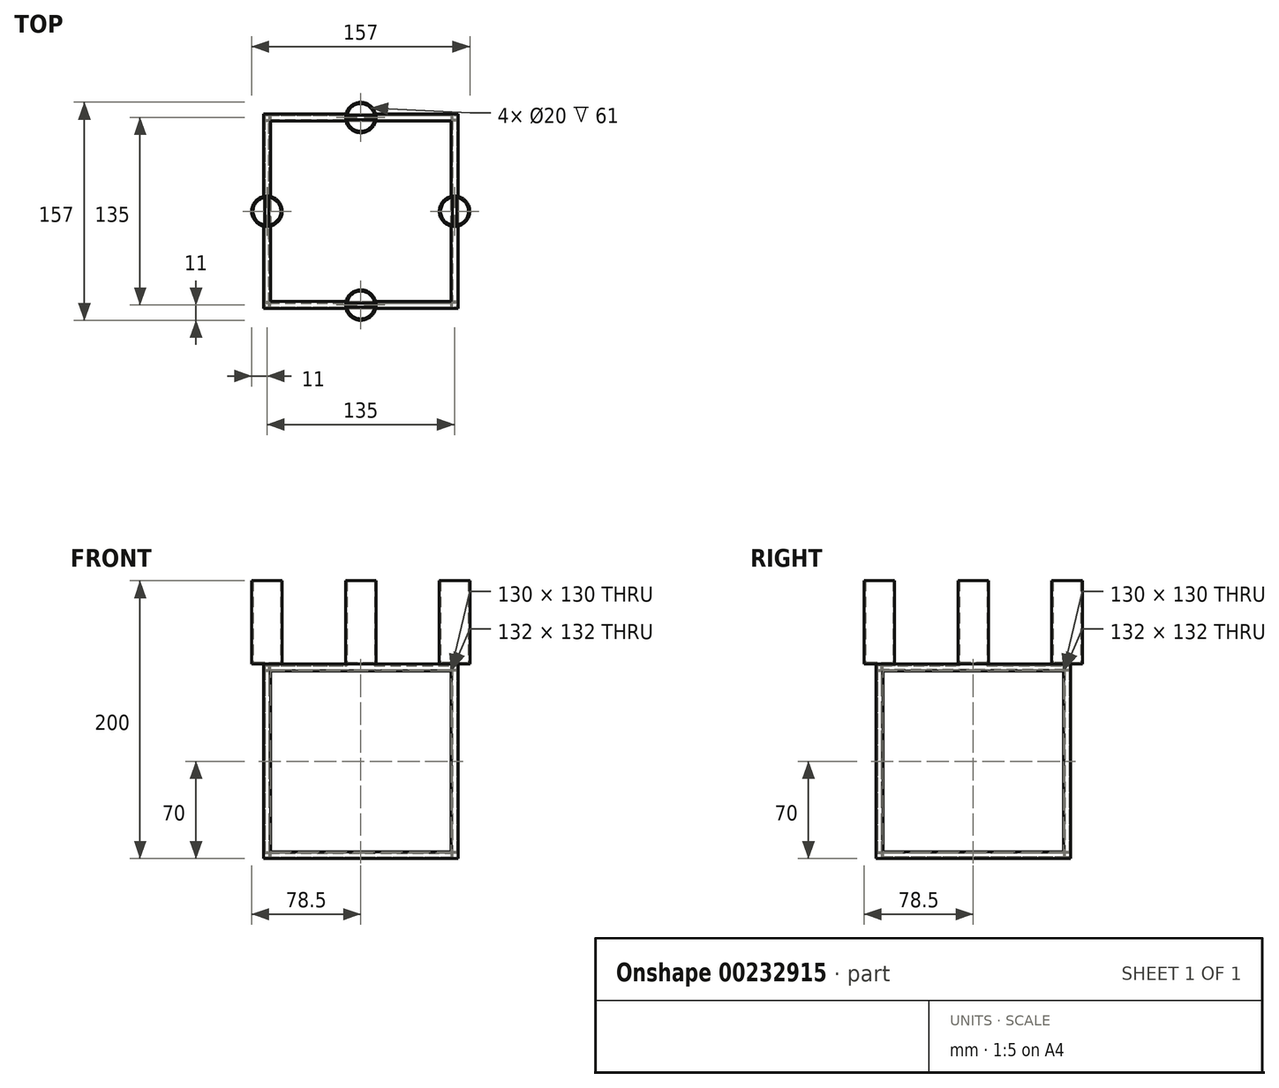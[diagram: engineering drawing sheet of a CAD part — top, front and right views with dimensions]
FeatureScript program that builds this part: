
annotation { "Feature Type Name" : "Feature", "Feature Type Description" : "" }
export const myFeature = defineFeature(function(context is Context, id is Id, definition is map)
    precondition{}
    {
        {
            var Q0;
            Q0=qCreatedBy(makeId("Top.planeOp"),FACE);
            var sketch = newSketch(context, id + "F0", { "sketchPlane" : qUnion([Q0])});
            skLineSegment(sketch, "E0.bottom", {"start": v(-70, 70) * mm, "end": v(70, 70) * mm});
            skLineSegment(sketch, "E0.top", {"start": v(-70, -70) * mm, "end": v(70, -70) * mm});
            skLineSegment(sketch, "E0.left", {"start": v(-70, 70) * mm, "end": v(-70, -70) * mm});
            skLineSegment(sketch, "E0.right", {"start": v(70, 70) * mm, "end": v(70, -70) * mm});
            skPoint(sketch, "E0.middle", {"position": v(0, 0) * mm});
            skLineSegment(sketch, "E1.0", {"start": v(-65, 65) * mm, "end": v(-65, -65) * mm});
            skLineSegment(sketch, "E1.1", {"start": v(-65, 65) * mm, "end": v(65, 65) * mm});
            skLineSegment(sketch, "E1.2", {"start": v(65, 65) * mm, "end": v(65, -65) * mm});
            skLineSegment(sketch, "E1.3", {"start": v(-65, -65) * mm, "end": v(65, -65) * mm});
            skLineSegment(sketch, "E2", {"start": v(-65, 65) * mm, "end": v(-70, 65) * mm});
            skLineSegment(sketch, "E3", {"start": v(-65, 65) * mm, "end": v(-65, 70) * mm});
            skLineSegment(sketch, "E4", {"start": v(65, 65) * mm, "end": v(70, 65) * mm});
            skLineSegment(sketch, "E5", {"start": v(65, 65) * mm, "end": v(65, 70) * mm});
            skLineSegment(sketch, "E6", {"start": v(65, 70) * mm, "end": v(65.55, 70.06) * mm});
            skLineSegment(sketch, "E7", {"start": v(65, -65) * mm, "end": v(70, -65) * mm});
            skLineSegment(sketch, "E8", {"start": v(65, -65) * mm, "end": v(65, -70) * mm});
            skLineSegment(sketch, "E9", {"start": v(-65, -65) * mm, "end": v(-70, -65) * mm});
            skLineSegment(sketch, "E10", {"start": v(-65, -65) * mm, "end": v(-65, -70) * mm});
            skLineSegment(sketch, "E11", {"start": v(-70, 65) * mm, "end": v(-70, 70) * mm});
            skLineSegment(sketch, "E12", {"start": v(-65, 70) * mm, "end": v(-65, 65) * mm});
            skLineSegment(sketch, "E13", {"start": v(-70, -70) * mm, "end": v(-70, -65) * mm});
            skLineSegment(sketch, "E14", {"start": v(65, -70) * mm, "end": v(70, -70) * mm});
            skLineSegment(sketch, "E15", {"start": v(70, 65) * mm, "end": v(70, 70) * mm});
            skSolve(sketch);
        }
        {
            var Q0;
            {var subQ4=sQuery(id+"F0.wireOp",EDGE,"E4");Q0=makeQuery(id+"F0.imprint","IMPRINT",FACE,{"disambiguationData":[TD([[makeQuery(id+"F0.imprint","IMPRINT",EDGE,{"derivedFrom":subQ4}),1.0]])]});}
            var Q1;
            {var subQ4=sQuery(id+"F0.wireOp",EDGE,"E9");Q1=makeQuery(id+"F0.imprint","IMPRINT",FACE,{"disambiguationData":[TD([[makeQuery(id+"F0.imprint","IMPRINT",EDGE,{"derivedFrom":subQ4}),1.0]])]});}
            var Q2;
            {var subQ4=sQuery(id+"F0.wireOp",EDGE,"E7");Q2=makeQuery(id+"F0.imprint","IMPRINT",FACE,{"disambiguationData":[TD([[makeQuery(id+"F0.imprint","IMPRINT",EDGE,{"derivedFrom":subQ4}),-1.0]])]});}
            var Q3;
            Q3=makeQuery(id+"F0.imprint","IMPRINT",FACE,{"disambiguationData":[TD([[makeQuery(id+"F0.imprint","IMPRINT",EDGE,{"derivedFrom":sQuery(id+"F0.wireOp",EDGE,"E1.1")}),1.0]])]});
            var Q4;
            Q4=makeQuery(id+"F0.imprint","IMPRINT",FACE,{"disambiguationData":[TD([[makeQuery(id+"F0.imprint","IMPRINT",EDGE,{"derivedFrom":sQuery(id+"F0.wireOp",EDGE,"E1.3")}),-1.0]])]});
            var Q5;
            Q5=makeQuery(id+"F0.imprint","IMPRINT",FACE,{"disambiguationData":[TD([[makeQuery(id+"F0.imprint","IMPRINT",EDGE,{"derivedFrom":sQuery(id+"F0.wireOp",EDGE,"E1.0")}),-1.0]])]});
            var Q6;
            Q6=makeQuery(id+"F0.imprint","IMPRINT",FACE,{"disambiguationData":[TD([[makeQuery(id+"F0.imprint","IMPRINT",EDGE,{"derivedFrom":sQuery(id+"F0.wireOp",EDGE,"E1.2")}),1.0]])]});
            var Q7;
            Q7=makeQuery(id+"F0.imprint","IMPRINT",FACE,{"disambiguationData":[TD([[makeQuery(id+"F0.imprint","IMPRINT",EDGE,{"derivedFrom":sQuery(id+"F0.wireOp",EDGE,"E2")}),-1.0]])]});
            extrude(context, id + "F1", {"entities" : qUnion([Q0, Q1, Q2, Q3, Q4, Q5, Q6, Q7]), "depth" : 5 * mm});
        }
        {
            var Q0;
            Q0=makeQuery(id+"F0.imprint","IMPRINT",FACE,{"disambiguationData":[TD([[makeQuery(id+"F0.imprint","IMPRINT",EDGE,{"derivedFrom":sQuery(id+"F0.wireOp",EDGE,"E2")}),-1.0]])]});
            var Q1;
            Q1=makeQuery(id+"F0.imprint","IMPRINT",FACE,{"disambiguationData":[TD([[makeQuery(id+"F0.imprint","IMPRINT",EDGE,{"derivedFrom":sQuery(id+"F0.wireOp",EDGE,"E9")}),1.0]])]});
            var Q2;
            {var subQ2=sQuery(id+"F0.wireOp",EDGE,"E7");Q2=makeQuery(id+"F0.imprint","IMPRINT",FACE,{"disambiguationData":[TD([[makeQuery(id+"F0.imprint","IMPRINT",EDGE,{"derivedFrom":subQ2}),-1.0]])]});}
            var Q3;
            Q3=makeQuery(id+"F0.imprint","IMPRINT",FACE,{"disambiguationData":[TD([[makeQuery(id+"F0.imprint","IMPRINT",EDGE,{"derivedFrom":sQuery(id+"F0.wireOp",EDGE,"E4")}),1.0]])]});
            extrude(context, id + "F2", {"entities" : qUnion([Q0, Q1, Q2, Q3]), "operationType" : NewBodyOperationType.ADD, "depth" : 140 * mm});
        }
        {
            var Q0;
            {var subQ0=sQuery(id+"F0.wireOp",EDGE,"E14");var subQ1=sQuery(id+"F0.wireOp",EDGE,"E0.top");Q0=makeQuery(id+"F2.boolean.opBoolean","MERGE",FACE,{"derivedFrom":[makeQuery(id+"F1.opExtrude","SWEPT_FACE",FACE,{"disambiguationData":[OSD([subQ1,subQ0])]}),makeQuery(id+"F2.opExtrude","SWEPT_FACE",FACE,{"disambiguationData":[OSD([subQ1])]}),makeQuery(id+"F2.opExtrude","SWEPT_FACE",FACE,{"disambiguationData":[OSD([subQ0])]})]});}
            var sketch = newSketch(context, id + "F3", { "sketchPlane" : qUnion([Q0])});
            skLineSegment(sketch, "E16", {"start": v(70, 140) * mm, "end": v(65, 140) * mm});
            skLineSegment(sketch, "E17", {"start": v(65, 140) * mm, "end": v(65, 135) * mm});
            skLineSegment(sketch, "E18", {"start": v(65, 135) * mm, "end": v(70, 135) * mm});
            skLineSegment(sketch, "E19", {"start": v(70, 135) * mm, "end": v(70, 140) * mm});
            skLineSegment(sketch, "E20", {"start": v(-70, 140) * mm, "end": v(-70, 135) * mm});
            skLineSegment(sketch, "E21", {"start": v(-70, 135) * mm, "end": v(-65, 135) * mm});
            skLineSegment(sketch, "E22", {"start": v(-65, 135) * mm, "end": v(-65, 140) * mm});
            skLineSegment(sketch, "E23", {"start": v(-65, 140) * mm, "end": v(-70, 140) * mm});
            skSolve(sketch);
        }
        {
            var Q0;
            Q0 = qSketchRegion(id + "F3", true);
            extrude(context, id + "F4", {"entities" : qUnion([Q0]), "operationType" : NewBodyOperationType.ADD, "oppositeDirection" : true, "depth" : 140 * mm});
        }
        {
            var Q0;
            {var subQ0=sQuery(id+"F0.wireOp",EDGE,"E15");var subQ1=sQuery(id+"F0.wireOp",EDGE,"E0.right");Q0=makeQuery(id+"F4.boolean.opBoolean","MERGE",FACE,{"derivedFrom":[makeQuery(id+"F2.boolean.opBoolean","MERGE",FACE,{"derivedFrom":[makeQuery(id+"F1.opExtrude","SWEPT_FACE",FACE,{"disambiguationData":[OSD([subQ1,subQ0])]}),makeQuery(id+"F2.opExtrude","SWEPT_FACE",FACE,{"disambiguationData":[OSD([subQ1])]}),makeQuery(id+"F2.opExtrude","SWEPT_FACE",FACE,{"disambiguationData":[OSD([subQ0])]})]}),makeQuery(id+"F4.opExtrude","SWEPT_FACE",FACE,{"disambiguationData":[OSD([sQuery(id+"F3.wireOp",EDGE,"E19")])]})]});}
            var sketch = newSketch(context, id + "F5", { "sketchPlane" : qUnion([Q0])});
            skLineSegment(sketch, "E24", {"start": v(-70, 140) * mm, "end": v(-65, 140) * mm});
            skLineSegment(sketch, "E25", {"start": v(-65, 140) * mm, "end": v(-65, 135) * mm});
            skLineSegment(sketch, "E26", {"start": v(-65, 135) * mm, "end": v(-70, 135) * mm});
            skLineSegment(sketch, "E27", {"start": v(-70, 135) * mm, "end": v(-70, 140) * mm});
            skLineSegment(sketch, "E28", {"start": v(65, 135) * mm, "end": v(70, 135) * mm});
            skLineSegment(sketch, "E29", {"start": v(70, 135) * mm, "end": v(70, 140) * mm});
            skLineSegment(sketch, "E30", {"start": v(70, 140) * mm, "end": v(65, 140) * mm});
            skLineSegment(sketch, "E31", {"start": v(65, 140) * mm, "end": v(65, 135) * mm});
            skSolve(sketch);
        }
        {
            var Q0;
            Q0 = qSketchRegion(id + "F5", true);
            extrude(context, id + "F6", {"entities" : qUnion([Q0]), "operationType" : NewBodyOperationType.ADD, "oppositeDirection" : true, "depth" : 140 * mm});
        }
        {
            var Q0;
            {var subQ0=sQuery(id+"F0.wireOp",EDGE,"E0.bottom");Q0=makeQuery(id+"F6.boolean.opBoolean","MERGE",FACE,{"derivedFrom":[makeQuery(id+"F4.boolean.opBoolean","MERGE",FACE,{"derivedFrom":[makeQuery(id+"F2.opExtrude","CAP_FACE",FACE,{"disambiguationData":[OSD([subQ0,sQuery(id+"F0.wireOp",EDGE,"E2"),sQuery(id+"F0.wireOp",EDGE,"E11"),sQuery(id+"F0.wireOp",EDGE,"E12")])],"isStart":false}),makeQuery(id+"F2.opExtrude","CAP_FACE",FACE,{"disambiguationData":[OSD([sQuery(id+"F0.wireOp",EDGE,"E0.top"),sQuery(id+"F0.wireOp",EDGE,"E9"),sQuery(id+"F0.wireOp",EDGE,"E10"),sQuery(id+"F0.wireOp",EDGE,"E13")])],"isStart":false}),makeQuery(id+"F4.opExtrude","SWEPT_FACE",FACE,{"disambiguationData":[OSD([sQuery(id+"F3.wireOp",EDGE,"E23")])]})]}),makeQuery(id+"F4.boolean.opBoolean","MERGE",FACE,{"derivedFrom":[makeQuery(id+"F2.opExtrude","CAP_FACE",FACE,{"disambiguationData":[OSD([subQ0,sQuery(id+"F0.wireOp",EDGE,"E4"),sQuery(id+"F0.wireOp",EDGE,"E5"),sQuery(id+"F0.wireOp",EDGE,"E15")])],"isStart":false}),makeQuery(id+"F2.opExtrude","CAP_FACE",FACE,{"disambiguationData":[OSD([sQuery(id+"F0.wireOp",EDGE,"E0.right"),sQuery(id+"F0.wireOp",EDGE,"E7"),sQuery(id+"F0.wireOp",EDGE,"E8"),sQuery(id+"F0.wireOp",EDGE,"E14")])],"isStart":false}),makeQuery(id+"F4.opExtrude","SWEPT_FACE",FACE,{"disambiguationData":[OSD([sQuery(id+"F3.wireOp",EDGE,"E16")])]})]}),makeQuery(id+"F6.opExtrude","SWEPT_FACE",FACE,{"disambiguationData":[OSD([sQuery(id+"F5.wireOp",EDGE,"E24")])]}),makeQuery(id+"F6.opExtrude","SWEPT_FACE",FACE,{"disambiguationData":[OSD([sQuery(id+"F5.wireOp",EDGE,"E30")])]})]});}
            var sketch = newSketch(context, id + "F7", { "sketchPlane" : qUnion([Q0])});
            skCircle(sketch, "E32", {"center": v(-67.5, 0) * mm, "radius": 11 * mm});
            skCircle(sketch, "E33", {"center": v(0, 67.5) * mm, "radius": 11 * mm});
            skPoint(sketch, "E33.centerSnap0", {"position": v(0, 65) * mm});
            skCircle(sketch, "E34", {"center": v(67.5, 0) * mm, "radius": 11 * mm});
            skCircle(sketch, "E35", {"center": v(0, -67.5) * mm, "radius": 11 * mm});
            skPoint(sketch, "E35.centerSnap0", {"position": v(0, -65) * mm});
            skSolve(sketch);
        }
        {
            var Q0;
            Q0 = qSketchRegion(id + "F7", true);
            extrude(context, id + "F8", {"entities" : qUnion([Q0]), "operationType" : NewBodyOperationType.ADD, "depth" : 60 * mm});
        }
        {
            var Q0;
            Q0=makeQuery(id+"F8.opExtrude","CAP_FACE",FACE,{"disambiguationData":[OSD([sQuery(id+"F7.wireOp",EDGE,"E33")])],"isStart":false});
            var Q1;
            Q1=makeQuery(id+"F8.opExtrude","CAP_FACE",FACE,{"disambiguationData":[OSD([sQuery(id+"F7.wireOp",EDGE,"E34")])],"isStart":false});
            var Q2;
            Q2=makeQuery(id+"F8.opExtrude","CAP_FACE",FACE,{"disambiguationData":[OSD([sQuery(id+"F7.wireOp",EDGE,"E35")])],"isStart":false});
            var Q3;
            Q3=makeQuery(id+"F8.opExtrude","CAP_FACE",FACE,{"disambiguationData":[OSD([sQuery(id+"F7.wireOp",EDGE,"E32")])],"isStart":false});
            shell(context, id + "F9", {"entities" : qUnion([Q0, Q1, Q2, Q3]), "thickness" : 1 * mm});
        }
    });
